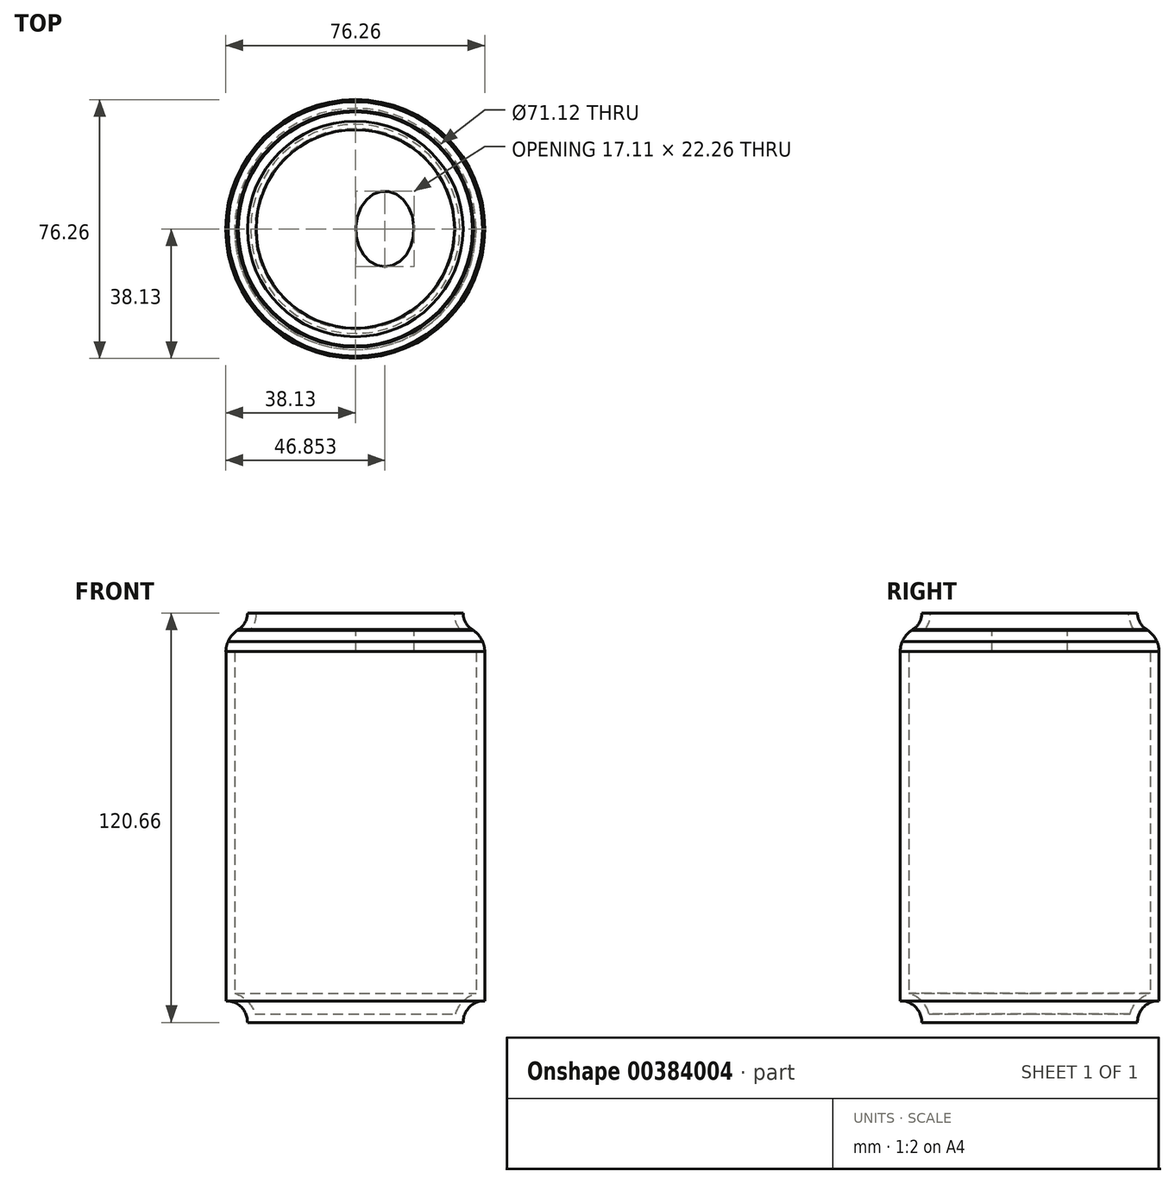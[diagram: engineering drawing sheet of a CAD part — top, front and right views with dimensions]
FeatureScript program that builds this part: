
annotation { "Feature Type Name" : "Feature", "Feature Type Description" : "" }
export const myFeature = defineFeature(function(context is Context, id is Id, definition is map)
    precondition{}
    {
        {
            var Q0;
            Q0=qCreatedBy(makeId("Front.planeOp"),FACE);
            var sketch = newSketch(context, id + "F0", { "sketchPlane" : qUnion([Q0])});
            skLineSegment(sketch, "E0.bottom", {"start": v(38.1, -53.98) * mm, "end": v(-38.1, -53.98) * mm});
            skLineSegment(sketch, "E0.top", {"start": v(38.1, 53.98) * mm, "end": v(-38.1, 53.97) * mm});
            skLineSegment(sketch, "E0.left", {"start": v(38.1, -53.98) * mm, "end": v(38.1, 53.98) * mm});
            skLineSegment(sketch, "E0.right", {"start": v(-38.1, -53.98) * mm, "end": v(-38.1, 53.97) * mm});
            skPoint(sketch, "E0.middle", {"position": v(0, 0) * mm});
            skLineSegment(sketch, "E1", {"start": v(-31.75, 60.32) * mm, "end": v(31.75, 60.33) * mm});
            skLineSegment(sketch, "E2", {"start": v(-31.75, -60.33) * mm, "end": v(31.75, -60.33) * mm});
            skFitSpline(sketch, "E3", {"points": [v(-38.1, 53.97) * mm, v(-31.75, 60.32) * mm], "startDerivative": vector(10.25, 3.3) * mm, "endDerivative": vector(0.03, 8.96) * mm});
            skFitSpline(sketch, "E4", {"points": [v(31.75, 60.33) * mm, v(38.1, 53.98) * mm], "startDerivative": vector(0.2, -9.8) * mm, "endDerivative": vector(12.6, -2.81) * mm});
            skFitSpline(sketch, "E5", {"points": [v(-38.1, -53.98) * mm, v(-31.75, -60.33) * mm], "startDerivative": vector(8.13, 0) * mm, "endDerivative": vector(0.48, -7.4) * mm});
            skFitSpline(sketch, "E6", {"points": [v(38.1, -53.98) * mm, v(31.75, -60.33) * mm], "startDerivative": vector(-12.36, 0) * mm, "endDerivative": vector(-0.05, -9.12) * mm});
            skLineSegment(sketch, "E7", {"start": v(0, -60.33) * mm, "end": v(0, 60.33) * mm});
            skSolve(sketch);
        }
        {
            var Q0;
            {var subQ0=sQuery(id+"F0.wireOp",EDGE,"E0.left");Q0=makeQuery(id+"F0.imprint","IMPRINT",FACE,{"disambiguationData":[TD([[makeQuery(id+"F0.imprint","IMPRINT",EDGE,{"derivedFrom":subQ0}),1.0]])]});}
            var Q1;
            {var subQ0=sQuery(id+"F0.wireOp",EDGE,"E4");Q1=makeQuery(id+"F0.imprint","IMPRINT",FACE,{"disambiguationData":[TD([[makeQuery(id+"F0.imprint","IMPRINT",EDGE,{"derivedFrom":subQ0}),-1.0]])]});}
            var Q2;
            {var subQ0=sQuery(id+"F0.wireOp",EDGE,"E6");Q2=makeQuery(id+"F0.imprint","IMPRINT",FACE,{"disambiguationData":[TD([[makeQuery(id+"F0.imprint","IMPRINT",EDGE,{"derivedFrom":subQ0}),-1.0]])]});}
            var Q3;
            Q3=sQuery(id+"F0.wireOp",EDGE,"E7");
            revolve(context, id + "F1", {"entities" : qUnion([Q0, Q1, Q2]), "axis" : qUnion([Q3]), "revolveType" : RevolveType.FULL});
        }
        {
            var Q0;
            Q0=makeQuery(id+"F1.opRevolve","SWEPT_EDGE",EDGE,{"disambiguationData":[OSD([sQuery(id+"F0.wireOp",EDGE,"E0.top"),sQuery(id+"F0.wireOp",EDGE,"E0.left"),sQuery(id+"F0.wireOp",EDGE,"E4")])]});
            fillet(context, id + "F2", {"entities" : qUnion([Q0]), "radius" : 7.62 * mm, "tangentPropagation" : true, "allowEdgeOverflow" : false});
        }
        {
            var Q0;
            Q0=makeQuery(id+"F1.opRevolve","SWEPT_FACE",FACE,{"disambiguationData":[OSD([sQuery(id+"F0.wireOp",EDGE,"E1")])]});
            shell(context, id + "F3", {"entities" : qUnion([Q0]), "thickness" : 2.54 * mm});
        }
        {
            var Q0;
            Q0=qCreatedBy(makeId("Front.planeOp"),FACE);
            var sketch = newSketch(context, id + "F4", { "sketchPlane" : qUnion([Q0])});
            skLineSegment(sketch, "E8", {"start": v(0, 55.4) * mm, "end": v(0, 48.95) * mm});
            skLineSegment(sketch, "E9", {"start": v(0, 48.95) * mm, "end": v(38.13, 48.95) * mm});
            skLineSegment(sketch, "E10", {"start": v(0, 55.4) * mm, "end": v(34.57, 55.4) * mm});
            skFitSpline(sketch, "E11", {"points": [v(34.57, 55.4) * mm, v(38.13, 48.95) * mm], "startDerivative": vector(9.52, -8.28) * mm, "endDerivative": vector(0.42, -6.12) * mm});
            skSolve(sketch);
        }
        {
            var Q0;
            Q0 = qSketchRegion(id + "F4", true);
            var Q1;
            Q1=sQuery(id+"F4.wireOp",EDGE,"E8");
            revolve(context, id + "F5", {"operationType" : NewBodyOperationType.ADD, "entities" : qUnion([Q0]), "axis" : qUnion([Q1]), "revolveType" : RevolveType.FULL});
        }
        {
            var Q0;
            Q0=qCreatedBy(makeId("Top.planeOp"),FACE);
            var sketch = newSketch(context, id + "F6", { "sketchPlane" : qUnion([Q0])});
            skEllipse(sketch, "E12", {"center": v(8.72, 0) * mm, "majorRadius": 11.13 * mm, "minorRadius": 8.56 * mm, "majorAxis": v(0, -1)});
            skSolve(sketch);
        }
        {
            var Q0;
            Q0 = qSketchRegion(id + "F6", true);
            var Q1;
            Q1=makeQuery(id+"F1.opRevolve","SWEPT_BODY",BODY,{"disambiguationData":[OSD([sQuery(id+"F0.wireOp",EDGE,"E0.left"),sQuery(id+"F0.wireOp",EDGE,"E1"),sQuery(id+"F0.wireOp",EDGE,"E2"),sQuery(id+"F0.wireOp",EDGE,"E4"),sQuery(id+"F0.wireOp",EDGE,"E6"),sQuery(id+"F0.wireOp",EDGE,"E7")])]});
            extrude(context, id + "F7", {"entities" : qUnion([Q0]), "operationType" : NewBodyOperationType.ADD, "endBoundEntityBody" : qUnion([Q1]), "depth" : 63.5 * mm});
        }
        {
            var Q0;
            Q0=makeQuery(id+"F7.opExtrude","CAP_FACE",FACE,{"disambiguationData":[OSD([sQuery(id+"F6.wireOp",EDGE,"E12")])],"isStart":false});
            extrude(context, id + "F8", {"entities" : qUnion([Q0]), "operationType" : NewBodyOperationType.REMOVE, "endBound" : BoundingType.UP_TO_NEXT, "oppositeDirection" : true, "depth" : 25.4 * mm});
        }
    });
